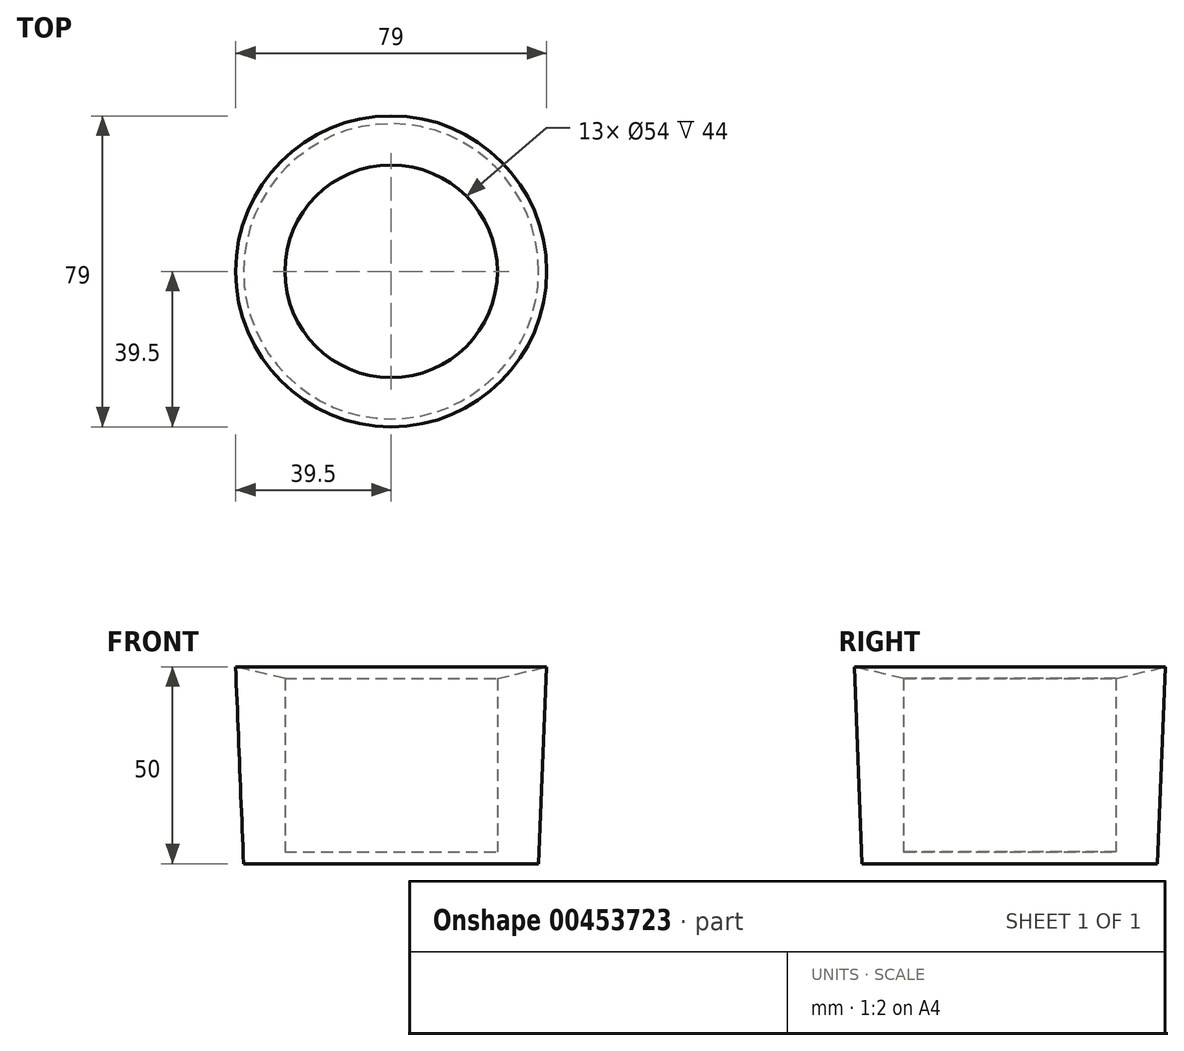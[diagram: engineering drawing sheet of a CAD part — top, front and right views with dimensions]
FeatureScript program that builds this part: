
annotation { "Feature Type Name" : "Feature", "Feature Type Description" : "" }
export const myFeature = defineFeature(function(context is Context, id is Id, definition is map)
    precondition{}
    {
        {
            var Q0;
            Q0=qCreatedBy(makeId("Right.planeOp"),FACE);
            var sketch = newSketch(context, id + "F0", { "sketchPlane" : qUnion([Q0])});
            skLineSegment(sketch, "E0", {"start": v(-39.5, 50) * mm, "end": v(-37.5, 0) * mm});
            skLineSegment(sketch, "E1", {"start": v(-37.5, 0) * mm, "end": v(0, 0) * mm});
            skLineSegment(sketch, "E2", {"start": v(0, 0) * mm, "end": v(0, 3) * mm});
            skLineSegment(sketch, "E3", {"start": v(0, 3) * mm, "end": v(-27, 3) * mm});
            skLineSegment(sketch, "E4", {"start": v(-27, 3) * mm, "end": v(-27, 47) * mm});
            skLineSegment(sketch, "E5", {"start": v(-27, 47) * mm, "end": v(-39.5, 50) * mm});
            skSolve(sketch);
        }
        {
            var Q0;
            Q0=makeQuery(id+"F0.imprint","IMPRINT",FACE,{"disambiguationData":[TD([[makeQuery(id+"F0.imprint","IMPRINT",EDGE,{"derivedFrom":sQuery(id+"F0.wireOp",EDGE,"E0")}),1.0]])]});
            var Q1;
            Q1=sQuery(id+"F0.wireOp",EDGE,"E2");
            revolve(context, id + "F1", {"entities" : qUnion([Q0]), "axis" : qUnion([Q1]), "revolveType" : RevolveType.FULL});
        }
    });
